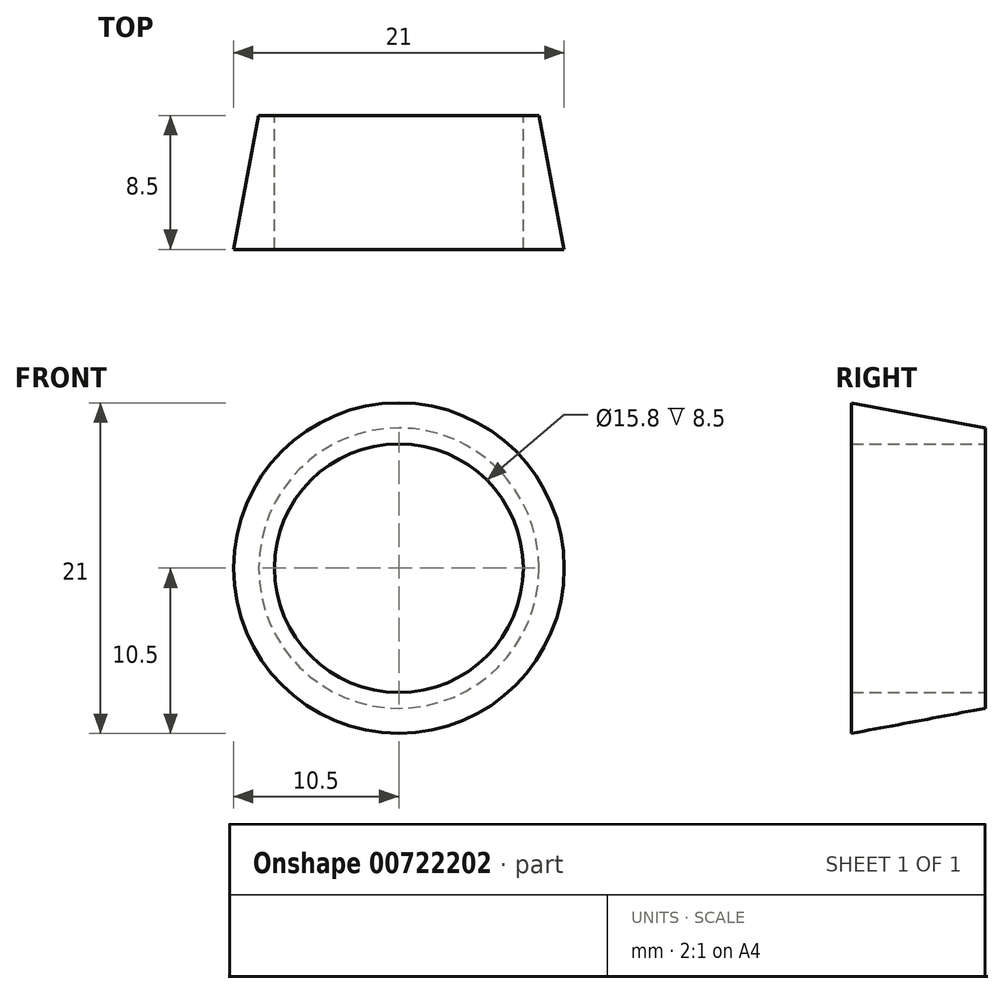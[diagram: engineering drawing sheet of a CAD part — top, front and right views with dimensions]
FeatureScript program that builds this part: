
annotation { "Feature Type Name" : "Feature", "Feature Type Description" : "" }
export const myFeature = defineFeature(function(context is Context, id is Id, definition is map)
    precondition{}
    {
        {
            var Q0;
            Q0=qCreatedBy(makeId("Front.planeOp"),FACE);
            var sketch = newSketch(context, id + "F0", { "sketchPlane" : qUnion([Q0])});
            skCircle(sketch, "E0", {"center": v(0, 0) * mm, "radius": 7.9 * mm, "construction": true});
            skCircle(sketch, "E1", {"center": v(0, 0) * mm, "radius": 8.9 * mm});
            skSolve(sketch);
        }
        {
            var Q0;
            Q0=qCreatedBy(makeId("Front.planeOp"),FACE);
            cPlane(context, id + "F1", {"entities" : qUnion([Q0]), "cplaneType" : CPlaneType.OFFSET, "offset" : 8.5 * mm, "width" : 150 * mm, "height" : 150 * mm});
        }
        {
            var Q0;
            Q0=qCreatedBy(id+"F1.planeOp",FACE);
            var sketch = newSketch(context, id + "F2", { "sketchPlane" : qUnion([Q0])});
            skCircle(sketch, "E2", {"center": v(0, 0) * mm, "radius": 10.5 * mm});
            skSolve(sketch);
        }
        {
            var Q0;
            Q0=makeQuery(id+"F0.imprint","IMPRINT",FACE,{"disambiguationData":[TD([[makeQuery(id+"F0.imprint","IMPRINT",EDGE,{"derivedFrom":sQuery(id+"F0.wireOp",EDGE,"E1")}),1.0]])]});
            var Q1;
            Q1=makeQuery(id+"F2.imprint","IMPRINT",FACE,{"disambiguationData":[TD([[makeQuery(id+"F2.imprint","IMPRINT",EDGE,{"derivedFrom":sQuery(id+"F2.wireOp",EDGE,"E2")}),1.0]])]});
            loft(context, id + "F3", {"sheetProfilesArray" : [{ "sheetProfileEntities" : qUnion([Q0]) }, { "sheetProfileEntities" : qUnion([Q1]) }]});
        }
        {
            var Q0;
            Q0=makeQuery(id+"F3.opLoft","CAP_FACE",FACE,{"disambiguationData":[OSD([makeQuery(id+"F0.imprint","IMPRINT",FACE,{"disambiguationData":[TD([[makeQuery(id+"F0.imprint","IMPRINT",EDGE,{"derivedFrom":sQuery(id+"F0.wireOp",EDGE,"E1")}),1.0]])]})])],"isStart":true});
            var sketch = newSketch(context, id + "F4", { "sketchPlane" : qUnion([Q0])});
            skCircle(sketch, "E3", {"center": v(0, 0) * mm, "radius": 7.9 * mm});
            skSolve(sketch);
        }
        {
            var Q0;
            Q0=makeQuery(id+"F4.imprint","IMPRINT",FACE,{"disambiguationData":[TD([[makeQuery(id+"F4.imprint","IMPRINT",EDGE,{"derivedFrom":sQuery(id+"F4.wireOp",EDGE,"E3")}),1.0]])]});
            extrude(context, id + "F5", {"entities" : qUnion([Q0]), "operationType" : NewBodyOperationType.REMOVE, "endBound" : BoundingType.THROUGH_ALL, "oppositeDirection" : true, "depth" : 25 * mm, "offsetDistance" : 25 * mm});
        }
    });
